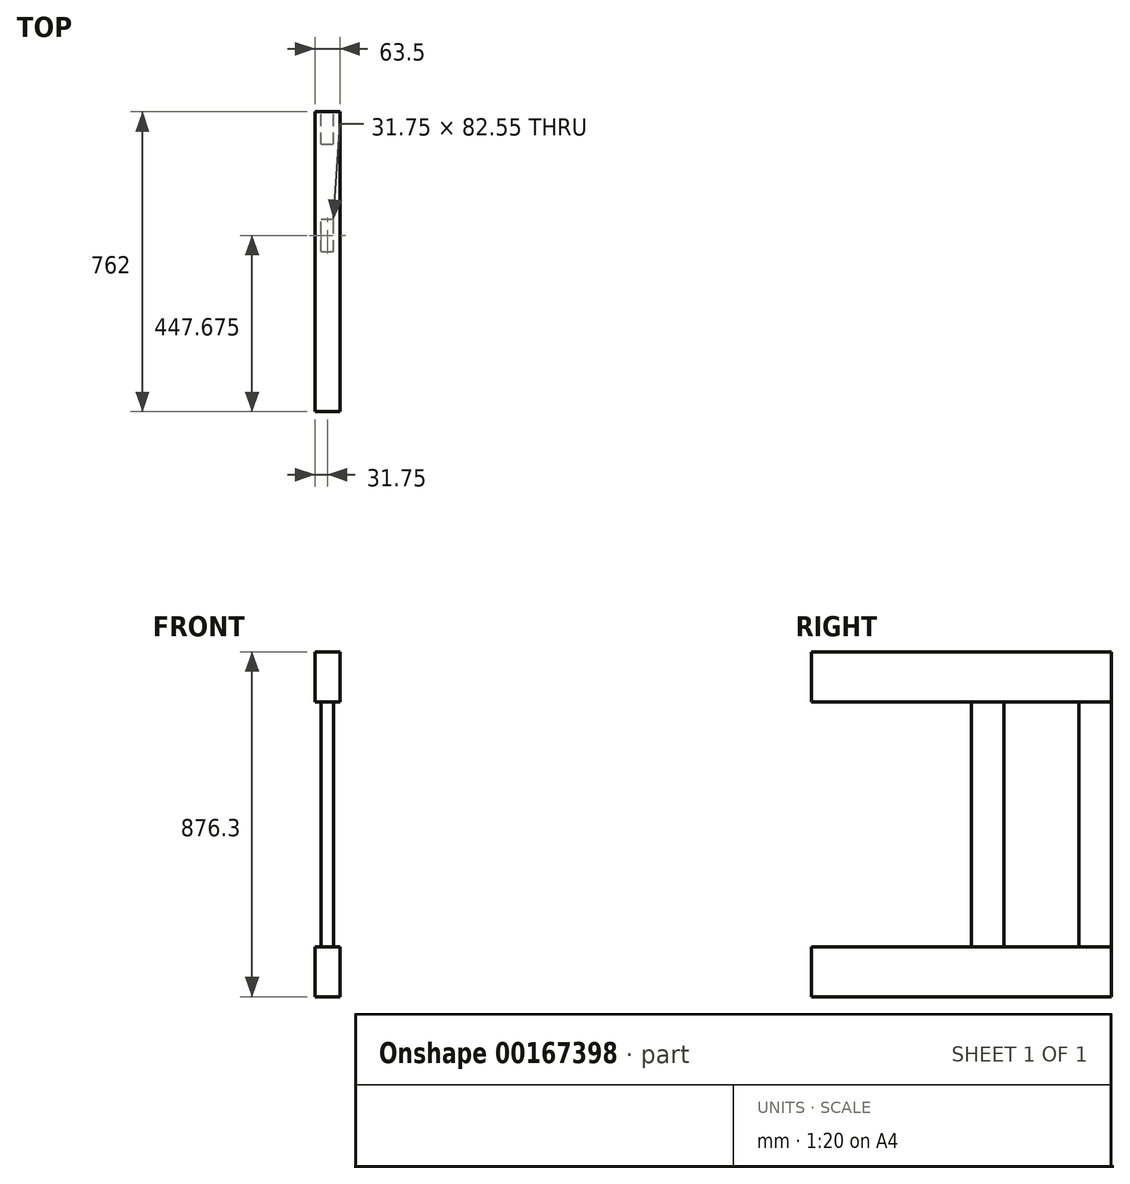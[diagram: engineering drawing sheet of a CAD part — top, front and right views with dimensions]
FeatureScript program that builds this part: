
annotation { "Feature Type Name" : "Feature", "Feature Type Description" : "" }
export const myFeature = defineFeature(function(context is Context, id is Id, definition is map)
    precondition{}
    {
        {
            var Q0;
            Q0=qCreatedBy(makeId("Right.planeOp"),FACE);
            var sketch = newSketch(context, id + "F0", { "sketchPlane" : qUnion([Q0])});
            skLineSegment(sketch, "E0.bottom", {"start": v(0, 0) * mm, "end": v(762, 0) * mm});
            skLineSegment(sketch, "E0.top", {"start": v(0, 127) * mm, "end": v(762, 127) * mm});
            skLineSegment(sketch, "E0.left", {"start": v(0, 0) * mm, "end": v(0, 127) * mm});
            skLineSegment(sketch, "E0.right", {"start": v(762, 0) * mm, "end": v(762, 127) * mm});
            skLineSegment(sketch, "E1.bottom", {"start": v(762, 749.3) * mm, "end": v(0, 749.3) * mm});
            skLineSegment(sketch, "E1.top", {"start": v(762, 876.3) * mm, "end": v(0, 876.3) * mm});
            skLineSegment(sketch, "E1.left", {"start": v(762, 749.3) * mm, "end": v(762, 876.3) * mm});
            skLineSegment(sketch, "E1.right", {"start": v(0, 749.3) * mm, "end": v(0, 876.3) * mm});
            skSolve(sketch);
        }
        {
            var Q0;
            Q0 = qSketchRegion(id + "F0", true);
            extrude(context, id + "F1", {"entities" : qUnion([Q0]), "endBound" : BoundingType.SYMMETRIC, "depth" : 63.5 * mm});
        }
        {
            var Q0;
            Q0=qCreatedBy(makeId("Right.planeOp"),FACE);
            var sketch = newSketch(context, id + "F2", { "sketchPlane" : qUnion([Q0])});
            skLineSegment(sketch, "E2.bottom", {"start": v(762, 0) * mm, "end": v(679.45, 0) * mm});
            skLineSegment(sketch, "E2.top", {"start": v(762, 876.3) * mm, "end": v(679.45, 876.3) * mm});
            skLineSegment(sketch, "E2.left", {"start": v(762, 0) * mm, "end": v(762, 876.3) * mm});
            skLineSegment(sketch, "E2.right", {"start": v(679.45, 0) * mm, "end": v(679.45, 876.3) * mm});
            skLineSegment(sketch, "E3.bottom", {"start": v(488.95, 0) * mm, "end": v(406.4, 0) * mm});
            skLineSegment(sketch, "E3.top", {"start": v(488.95, 876.3) * mm, "end": v(406.4, 876.3) * mm});
            skLineSegment(sketch, "E3.left", {"start": v(488.95, 0) * mm, "end": v(488.95, 876.3) * mm});
            skLineSegment(sketch, "E3.right", {"start": v(406.4, 0) * mm, "end": v(406.4, 876.3) * mm});
            skSolve(sketch);
        }
        {
            var Q0;
            Q0 = qSketchRegion(id + "F2", true);
            extrude(context, id + "F3", {"entities" : qUnion([Q0]), "operationType" : NewBodyOperationType.ADD, "endBound" : BoundingType.SYMMETRIC, "depth" : 31.75 * mm});
        }
    });
